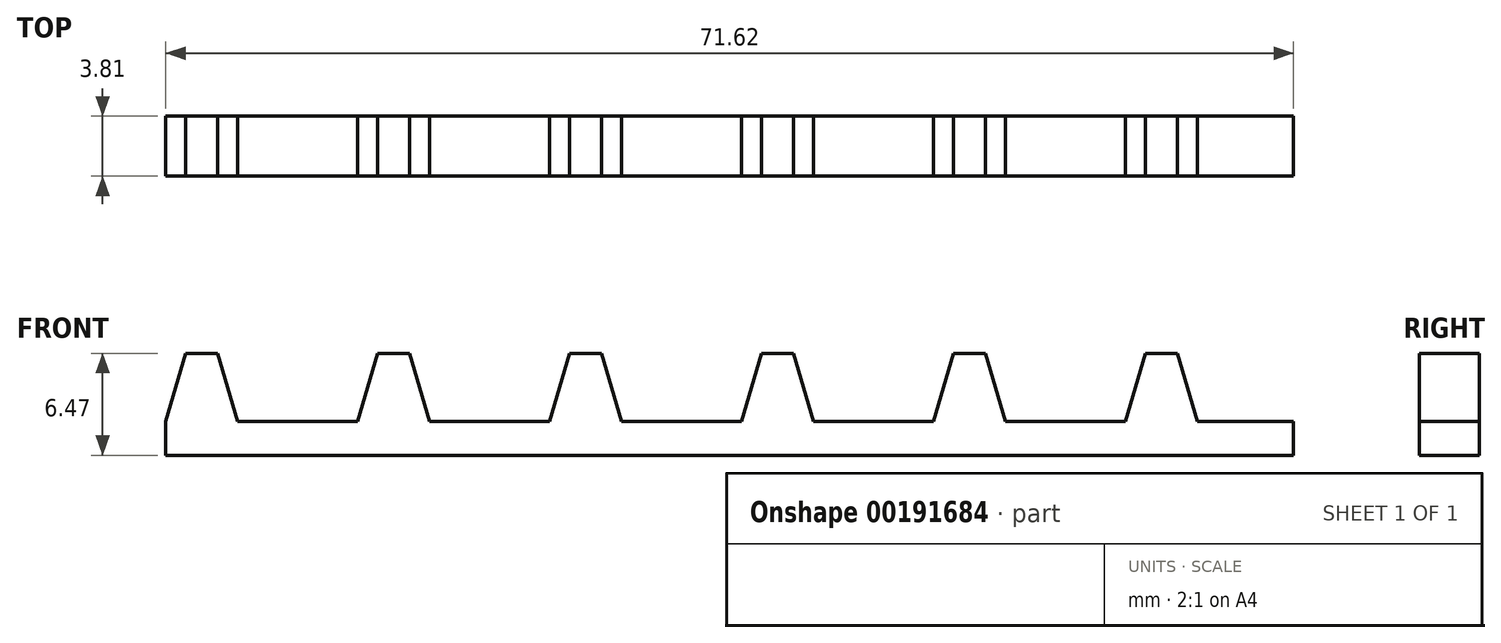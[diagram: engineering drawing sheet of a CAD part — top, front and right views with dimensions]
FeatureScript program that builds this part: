
annotation { "Feature Type Name" : "Feature", "Feature Type Description" : "" }
export const myFeature = defineFeature(function(context is Context, id is Id, definition is map)
    precondition{}
    {
        {
            var Q0;
            Q0=qCreatedBy(makeId("Front.planeOp"),FACE);
            var sketch = newSketch(context, id + "F0", { "sketchPlane" : qUnion([Q0])});
            skLineSegment(sketch, "E0.bottom", {"start": v(-38.44, 14.74) * mm, "end": v(33.18, 14.74) * mm});
            skLineSegment(sketch, "E0.top", {"start": v(-38.44, 16.9) * mm, "end": v(33.18, 16.9) * mm});
            skLineSegment(sketch, "E0.left", {"start": v(-38.44, 14.74) * mm, "end": v(-38.44, 16.9) * mm});
            skLineSegment(sketch, "E1", {"start": v(-38.44, 16.9) * mm, "end": v(-37.17, 21.21) * mm});
            skLineSegment(sketch, "E2", {"start": v(-37.17, 21.21) * mm, "end": v(-35.14, 21.21) * mm});
            skLineSegment(sketch, "E3", {"start": v(-35.14, 21.21) * mm, "end": v(-33.87, 16.9) * mm});
            skLineSegment(sketch, "E4", {"start": v(-38.44, 16.9) * mm, "end": v(-33.87, 16.9) * mm});
            skLineSegment(sketch, "E5", {"start": v(-36.16, 21.21) * mm, "end": v(-36.16, 16.9) * mm, "construction": true});
            skLineSegment(sketch, "E6", {"start": v(33.18, 14.74) * mm, "end": v(33.18, 16.9) * mm});
            skLineSegment(sketch, "E7.1.0.0", {"start": v(-22.95, 21.21) * mm, "end": v(-21.68, 16.9) * mm});
            skLineSegment(sketch, "E7.1.0.1", {"start": v(-26.25, 16.9) * mm, "end": v(-24.98, 21.21) * mm});
            skLineSegment(sketch, "E7.1.0.2", {"start": v(-24.98, 21.21) * mm, "end": v(-22.95, 21.21) * mm});
            skLineSegment(sketch, "E7.2.0.0", {"start": v(-10.76, 21.21) * mm, "end": v(-9.49, 16.9) * mm});
            skLineSegment(sketch, "E7.2.0.1", {"start": v(-14.06, 16.9) * mm, "end": v(-12.8, 21.21) * mm});
            skLineSegment(sketch, "E7.2.0.2", {"start": v(-12.8, 21.21) * mm, "end": v(-10.76, 21.21) * mm});
            skLineSegment(sketch, "E7.3.0.0", {"start": v(1.43, 21.21) * mm, "end": v(2.7, 16.9) * mm});
            skLineSegment(sketch, "E7.3.0.1", {"start": v(-1.87, 16.9) * mm, "end": v(-0.6, 21.21) * mm});
            skLineSegment(sketch, "E7.3.0.2", {"start": v(-0.6, 21.21) * mm, "end": v(1.43, 21.21) * mm});
            skLineSegment(sketch, "E7.4.0.0", {"start": v(13.63, 21.21) * mm, "end": v(14.9, 16.9) * mm});
            skLineSegment(sketch, "E7.4.0.1", {"start": v(10.32, 16.9) * mm, "end": v(11.6, 21.21) * mm});
            skLineSegment(sketch, "E7.4.0.2", {"start": v(11.6, 21.21) * mm, "end": v(13.63, 21.21) * mm});
            skLineSegment(sketch, "E7.5.0.0", {"start": v(25.82, 21.21) * mm, "end": v(27.09, 16.9) * mm});
            skLineSegment(sketch, "E7.5.0.1", {"start": v(22.52, 16.9) * mm, "end": v(23.79, 21.21) * mm});
            skLineSegment(sketch, "E7.5.0.2", {"start": v(23.79, 21.21) * mm, "end": v(25.82, 21.21) * mm});
            skLineSegment(sketch, "E7.direction1", {"start": v(-38.44, 16.9) * mm, "end": v(-26.25, 16.9) * mm, "construction": true});
            skPoint(sketch, "E8.centerSnap0", {"position": v(-38.44, 15.82) * mm});
            skSolve(sketch);
        }
        {
            var Q0;
            Q0=qSketchRegion(id+"F0",true);
            extrude(context, id + "F1", {"entities" : qUnion([Q0]), "depth" : 3.8 * mm});
        }
        {
            var Q0;
            Q0=qCreatedBy(makeId("Right.planeOp"),FACE);
            var Q1;
            Q1=makeQuery(id+"F1.opExtrude","CAP_VERTEX",VERTEX,{"disambiguationData":[OSD([sQuery(id+"F0.wireOp",EDGE,"E0.bottom"),sQuery(id+"F0.wireOp",EDGE,"E6")])],"isStart":false});
            cPlane(context, id + "F2", {"entities" : qUnion([Q0, Q1]), "cplaneType" : CPlaneType.PLANE_POINT, "offset" : 25.4 * mm, "width" : 152.4 * mm, "height" : 152.4 * mm});
        }
    });
